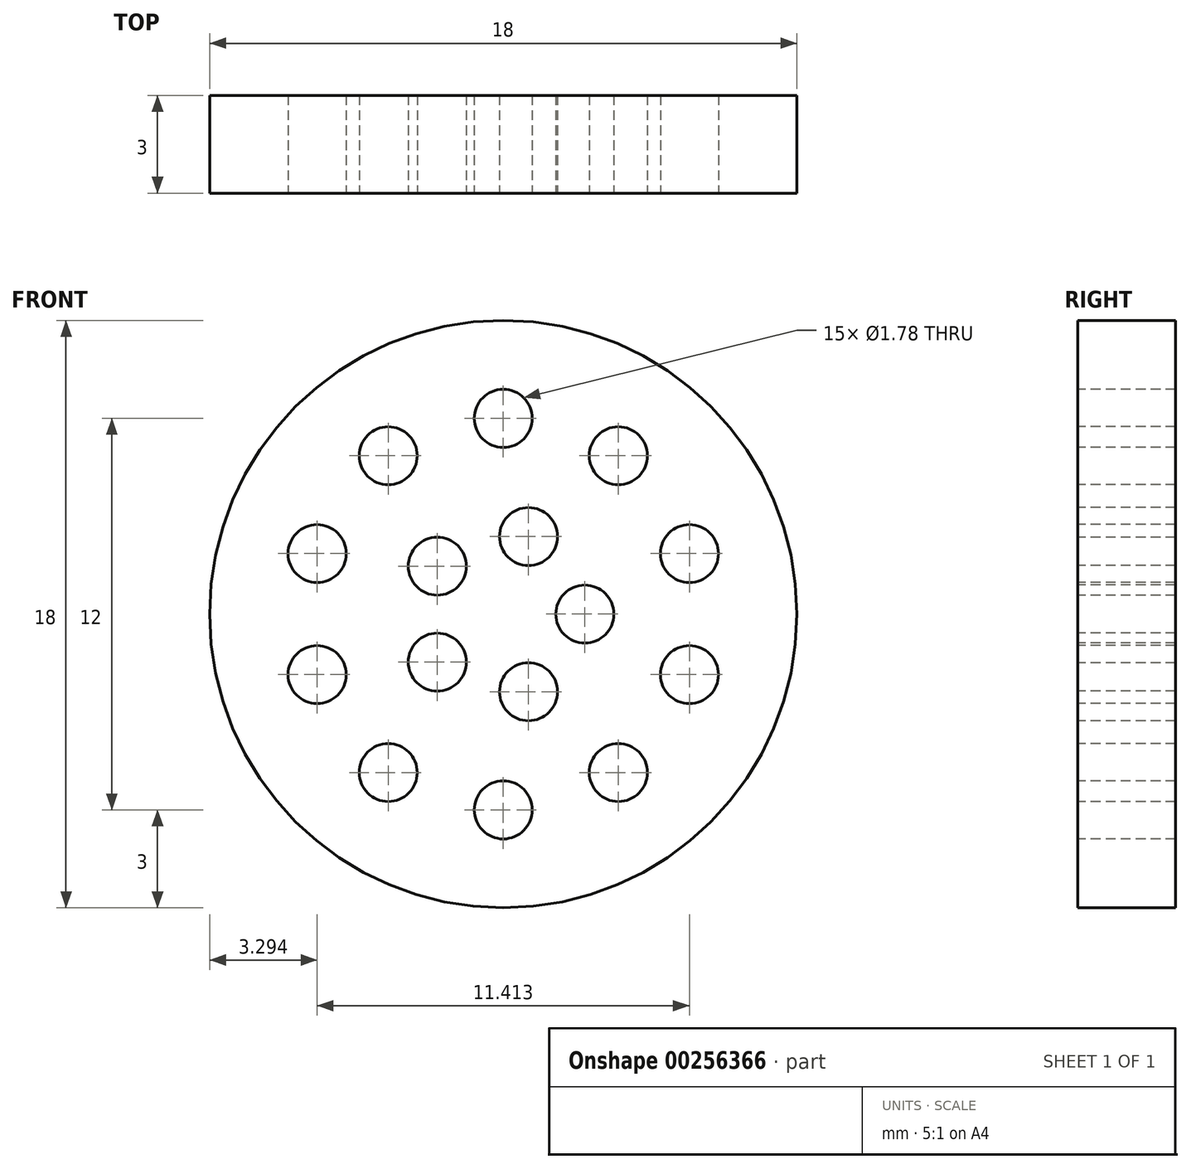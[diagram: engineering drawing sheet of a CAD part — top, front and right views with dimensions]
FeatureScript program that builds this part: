
annotation { "Feature Type Name" : "Feature", "Feature Type Description" : "" }
export const myFeature = defineFeature(function(context is Context, id is Id, definition is map)
    precondition{}
    {
        {
            var Q0;
            Q0=qCreatedBy(makeId("Front.planeOp"),FACE);
            var sketch = newSketch(context, id + "F0", { "sketchPlane" : qUnion([Q0])});
            skCircle(sketch, "E0", {"center": v(0, 0) * mm, "radius": 9 * mm});
            skSolve(sketch);
        }
        {
            var Q0;
            Q0 = qSketchRegion(id + "F0", true);
            extrude(context, id + "F1", {"entities" : qUnion([Q0]), "depth" : 3 * mm});
        }
        {
            var Q0;
            Q0=makeQuery(id+"F1.opExtrude","CAP_FACE",FACE,{"disambiguationData":[OSD([sQuery(id+"F0.wireOp",EDGE,"E0")])],"isStart":false});
            var sketch = newSketch(context, id + "F2", { "sketchPlane" : qUnion([Q0])});
            skCircle(sketch, "E1", {"center": v(0, 0) * mm, "radius": 6 * mm});
            skCircle(sketch, "E2", {"center": v(0, 0) * mm, "radius": 2.5 * mm});
            skPoint(sketch, "E3", {"position": v(0, 6) * mm});
            skPoint(sketch, "E4.1.0", {"position": v(-3.53, 4.85) * mm});
            skPoint(sketch, "E4.2.0", {"position": v(-5.7, 1.85) * mm});
            skPoint(sketch, "E4.3.0", {"position": v(-5.7, -1.85) * mm});
            skPoint(sketch, "E4.4.0", {"position": v(-3.53, -4.85) * mm});
            skPoint(sketch, "E4.5.0", {"position": v(0, -6) * mm});
            skPoint(sketch, "E4.6.0", {"position": v(3.53, -4.85) * mm});
            skPoint(sketch, "E4.7.0", {"position": v(5.7, -1.85) * mm});
            skPoint(sketch, "E5.0.8.0", {"position": v(5.7, 1.85) * mm});
            skPoint(sketch, "E5.0.9.0", {"position": v(3.53, 4.85) * mm});
            skPoint(sketch, "E6", {"position": v(2.5, 0) * mm});
            skPoint(sketch, "E7.1.0", {"position": v(0.77, 2.38) * mm});
            skPoint(sketch, "E7.2.0", {"position": v(-2.02, 1.47) * mm});
            skPoint(sketch, "E7.3.0", {"position": v(-2.02, -1.47) * mm});
            skPoint(sketch, "E7.4.0", {"position": v(0.77, -2.38) * mm});
            skSolve(sketch);
        }
        {
            var Q0;
            Q0=sQuery(id+"F2.wireOp",VERTEX,"IZkkXyyh-uieR-OPkv-T1By-iHbS7jxYazU4.center");
            var Q1;
            Q1=sQuery(id+"F2.wireOp",VERTEX,"e5d7f120-e1ad-4062-a4dd-eb10c04244b4.1.0");
            var Q2;
            Q2=sQuery(id+"F2.wireOp",VERTEX,"a3fc0f77-ada5-4d6e-a54e-82b45d77d4ef");
            var Q3;
            Q3=sQuery(id+"F2.wireOp",VERTEX,"e5d7f120-e1ad-4062-a4dd-eb10c04244b4.15.0");
            var Q4;
            Q4=sQuery(id+"F2.wireOp",VERTEX,"e5d7f120-e1ad-4062-a4dd-eb10c04244b4.14.0");
            var Q5;
            Q5=sQuery(id+"F2.wireOp",VERTEX,"e5d7f120-e1ad-4062-a4dd-eb10c04244b4.13.0");
            var Q6;
            Q6=sQuery(id+"F2.wireOp",VERTEX,"e5d7f120-e1ad-4062-a4dd-eb10c04244b4.12.0");
            var Q7;
            Q7=sQuery(id+"F2.wireOp",VERTEX,"e5d7f120-e1ad-4062-a4dd-eb10c04244b4.11.0");
            var Q8;
            Q8=sQuery(id+"F2.wireOp",VERTEX,"e5d7f120-e1ad-4062-a4dd-eb10c04244b4.10.0");
            var Q9;
            Q9=sQuery(id+"F2.wireOp",VERTEX,"e5d7f120-e1ad-4062-a4dd-eb10c04244b4.9.0");
            var Q10;
            Q10=sQuery(id+"F2.wireOp",VERTEX,"e5d7f120-e1ad-4062-a4dd-eb10c04244b4.8.0");
            var Q11;
            Q11=sQuery(id+"F2.wireOp",VERTEX,"e5d7f120-e1ad-4062-a4dd-eb10c04244b4.7.0");
            var Q12;
            Q12=sQuery(id+"F2.wireOp",VERTEX,"e5d7f120-e1ad-4062-a4dd-eb10c04244b4.6.0");
            var Q13;
            Q13=sQuery(id+"F2.wireOp",VERTEX,"e5d7f120-e1ad-4062-a4dd-eb10c04244b4.5.0");
            var Q14;
            Q14=sQuery(id+"F2.wireOp",VERTEX,"e5d7f120-e1ad-4062-a4dd-eb10c04244b4.4.0");
            var Q15;
            Q15=sQuery(id+"F2.wireOp",VERTEX,"e5d7f120-e1ad-4062-a4dd-eb10c04244b4.3.0");
            var Q16;
            Q16=sQuery(id+"F2.wireOp",VERTEX,"e5d7f120-e1ad-4062-a4dd-eb10c04244b4.2.0");
            var Q17;
            Q17=sQuery(id+"F2.wireOp",VERTEX,"E4.1.0");
            var Q18;
            Q18=sQuery(id+"F2.wireOp",VERTEX,"E4.2.0");
            var Q19;
            Q19=sQuery(id+"F2.wireOp",VERTEX,"E4.3.0");
            var Q20;
            Q20=sQuery(id+"F2.wireOp",VERTEX,"E4.4.0");
            var Q21;
            Q21=sQuery(id+"F2.wireOp",VERTEX,"E4.5.0");
            var Q22;
            Q22=sQuery(id+"F2.wireOp",VERTEX,"E4.6.0");
            var Q23;
            Q23=sQuery(id+"F2.wireOp",VERTEX,"E4.7.0");
            var Q24;
            Q24=sQuery(id+"F2.wireOp",VERTEX,"E3");
            var Q25;
            Q25=sQuery(id+"F2.wireOp",VERTEX,"fe61b65a-4676-42ba-b70b-1be49e719168");
            var Q26;
            Q26=sQuery(id+"F2.wireOp",VERTEX,"41a6d257-8674-4c30-ae07-6221aaa3ded3.1.0");
            var Q27;
            Q27=sQuery(id+"F2.wireOp",VERTEX,"41a6d257-8674-4c30-ae07-6221aaa3ded3.2.0");
            var Q28;
            Q28=sQuery(id+"F2.wireOp",VERTEX,"41a6d257-8674-4c30-ae07-6221aaa3ded3.3.0");
            var Q29;
            Q29=sQuery(id+"F2.wireOp",VERTEX,"E7.2.0");
            var Q30;
            Q30=sQuery(id+"F2.wireOp",VERTEX,"E7.3.0");
            var Q31;
            Q31=sQuery(id+"F2.wireOp",VERTEX,"E7.4.0");
            var Q32;
            Q32=sQuery(id+"F2.wireOp",VERTEX,"E6");
            var Q33;
            Q33=sQuery(id+"F2.wireOp",VERTEX,"E7.1.0");
            var Q34;
            Q34=sQuery(id+"F2.wireOp",VERTEX,"E5.0.9.0");
            var Q35;
            Q35=sQuery(id+"F2.wireOp",VERTEX,"E5.0.8.0");
            var Q36;
            Q36=makeQuery(id+"F1.opExtrude","SWEPT_BODY",BODY,{"disambiguationData":[OSD([sQuery(id+"F0.wireOp",EDGE,"E0")])]});
            hole(context, id + "F3", {"style" : HoleStyle.SIMPLE, "endStyle" : HoleEndStyle.BLIND, "standardTappedOrClearance" : lookupTablePath({ "standard" : "ANSI", "fit" : "Normal (ASME)", "size" : "#0", "type" : "Clearance" }), "standardBlindInLast" : lookupTablePath({ "fit" : "Free", "standard" : "ANSI", "size" : "#0", "type" : "Clearance" }), "holeDiameter" : 1.78 * mm, "holeDepth" : 15 * mm, "tappedDepth" : 12 * mm, "tapClearance" : 3, "locations" : qUnion([Q0, Q1, Q2, Q3, Q4, Q5, Q6, Q7, Q8, Q9, Q10, Q11, Q12, Q13, Q14, Q15, Q16, Q17, Q18, Q19, Q20, Q21, Q22, Q23, Q24, Q25, Q26, Q27, Q28, Q29, Q30, Q31, Q32, Q33, Q34, Q35]), "scope" : qUnion([Q36])});
        }
    });
